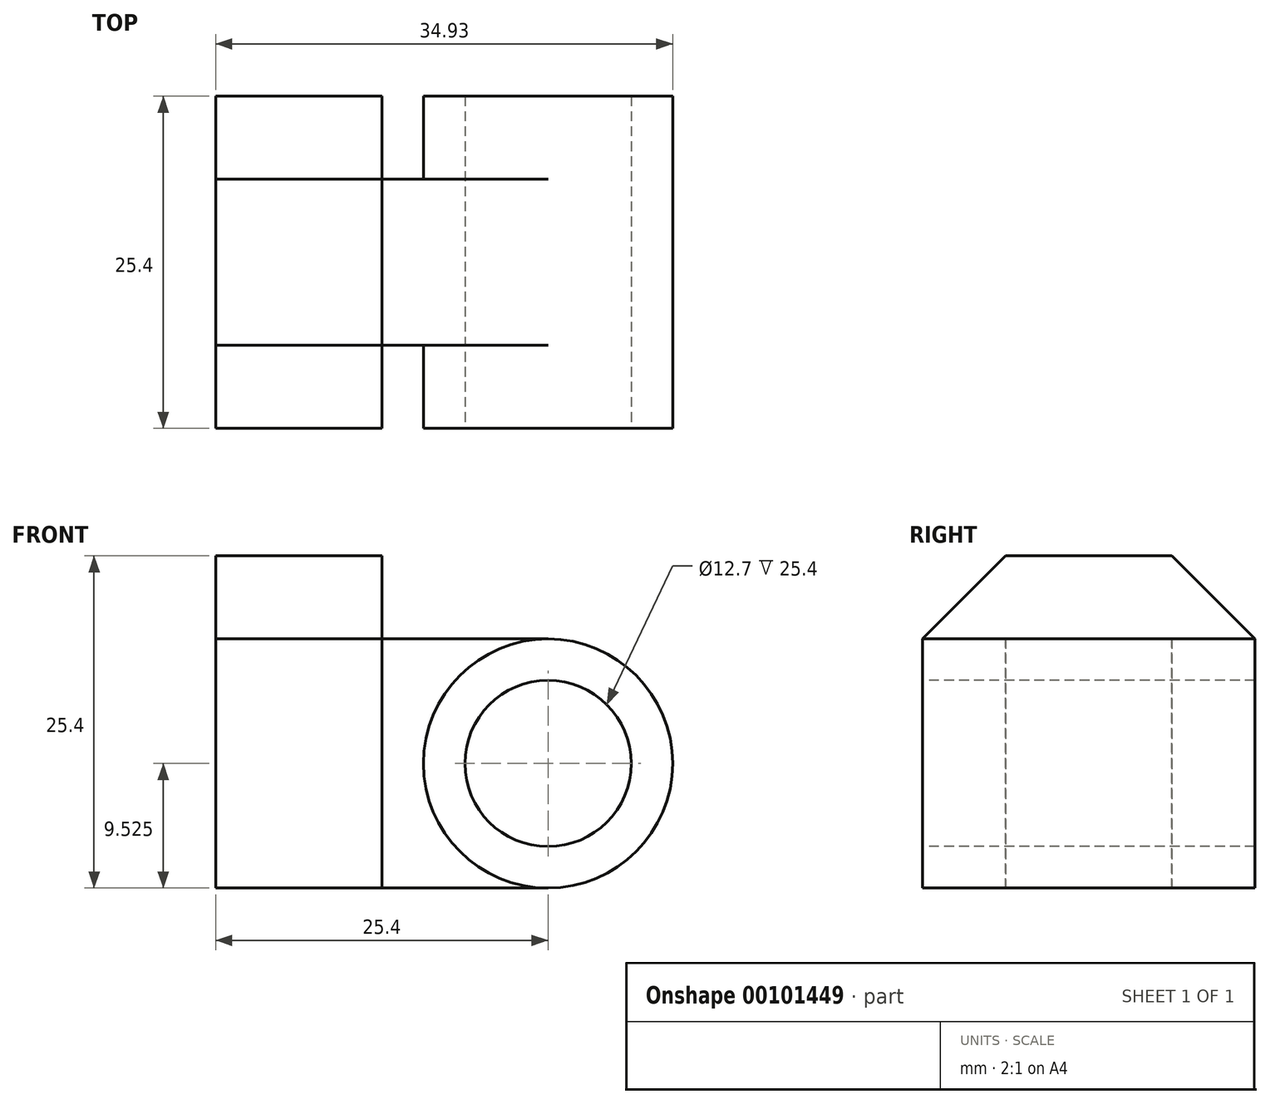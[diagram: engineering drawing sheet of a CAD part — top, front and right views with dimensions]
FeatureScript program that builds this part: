
annotation { "Feature Type Name" : "Feature", "Feature Type Description" : "" }
export const myFeature = defineFeature(function(context is Context, id is Id, definition is map)
    precondition{}
    {
        {
            var Q0;
            Q0=qCreatedBy(makeId("Right.planeOp"),FACE);
            var sketch = newSketch(context, id + "F0", { "sketchPlane" : qUnion([Q0])});
            skLineSegment(sketch, "E0", {"start": v(0, 0) * mm, "end": v(25.4, 0) * mm});
            skLineSegment(sketch, "E1", {"start": v(25.4, 0) * mm, "end": v(25.4, 19.05) * mm});
            skLineSegment(sketch, "E2", {"start": v(25.4, 19.05) * mm, "end": v(19.05, 25.4) * mm});
            skLineSegment(sketch, "E3", {"start": v(19.05, 25.4) * mm, "end": v(6.35, 25.4) * mm});
            skLineSegment(sketch, "E4", {"start": v(6.35, 25.4) * mm, "end": v(0, 19.05) * mm});
            skLineSegment(sketch, "E5", {"start": v(0, 19.05) * mm, "end": v(0, 0) * mm});
            skSolve(sketch);
        }
        {
            var Q0;
            Q0 = qSketchRegion(id + "F0", true);
            extrude(context, id + "F1", {"entities" : qUnion([Q0]), "depth" : 12.7 * mm});
        }
        {
            var Q0;
            Q0=qCreatedBy(makeId("Front.planeOp"),FACE);
            var sketch = newSketch(context, id + "F2", { "sketchPlane" : qUnion([Q0])});
            skLineSegment(sketch, "E6", {"start": v(0, 0) * mm, "end": v(25.4, 0) * mm, "construction": true});
            skLineSegment(sketch, "E7", {"start": v(25.4, 0) * mm, "end": v(25.4, 9.53) * mm, "construction": true});
            skCircle(sketch, "E8", {"center": v(25.4, 9.53) * mm, "radius": 6.35 * mm});
            skCircle(sketch, "E9", {"center": v(25.4, 9.53) * mm, "radius": 9.53 * mm});
            skSolve(sketch);
        }
        {
            var Q0;
            Q0 = qSketchRegion(id + "F2", true);
            extrude(context, id + "F3", {"entities" : qUnion([Q0]), "oppositeDirection" : true, "depth" : 25.4 * mm});
        }
        {
            var Q0;
            Q0=makeQuery(id+"F1.opExtrude","CAP_FACE",FACE,{"disambiguationData":[OSD([sQuery(id+"F0.wireOp",EDGE,"E0"),sQuery(id+"F0.wireOp",EDGE,"E1"),sQuery(id+"F0.wireOp",EDGE,"E2"),sQuery(id+"F0.wireOp",EDGE,"E3"),sQuery(id+"F0.wireOp",EDGE,"E4"),sQuery(id+"F0.wireOp",EDGE,"E5")])],"isStart":false});
            var sketch = newSketch(context, id + "F4", { "sketchPlane" : qUnion([Q0])});
            skLineSegment(sketch, "E10", {"start": v(12.7, 0) * mm, "end": v(19.05, 0) * mm});
            skLineSegment(sketch, "E11", {"start": v(19.05, 0) * mm, "end": v(19.05, 19.05) * mm});
            skLineSegment(sketch, "E12", {"start": v(19.05, 19.05) * mm, "end": v(6.35, 19.05) * mm});
            skLineSegment(sketch, "E13", {"start": v(6.35, 19.05) * mm, "end": v(6.35, 0) * mm});
            skLineSegment(sketch, "E14", {"start": v(6.35, 0) * mm, "end": v(12.7, 0) * mm});
            skSolve(sketch);
        }
        {
            var Q0;
            Q0 = qSketchRegion(id + "F4", true);
            var Q1;
            Q1=makeQuery(id+"F3.opExtrude","SWEPT_FACE",FACE,{"disambiguationData":[OSD([sQuery(id+"F2.wireOp",EDGE,"E9")])]});
            extrude(context, id + "F5", {"entities" : qUnion([Q0]), "operationType" : NewBodyOperationType.ADD, "endBound" : BoundingType.UP_TO_SURFACE, "endBoundEntityFace" : qUnion([Q1]), "depth" : 25.4 * mm});
        }
    });
